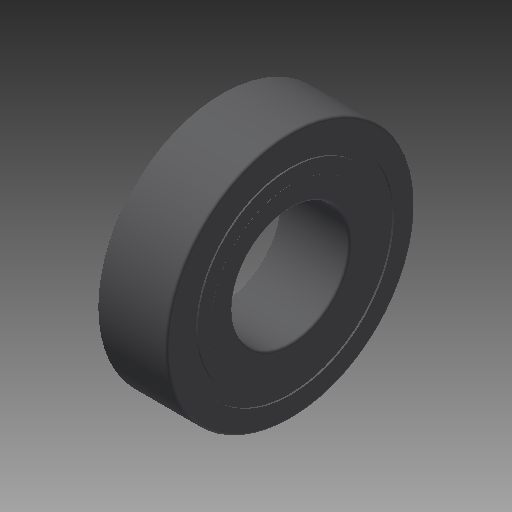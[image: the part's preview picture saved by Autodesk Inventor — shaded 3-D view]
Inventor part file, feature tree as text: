
AUTODESK INVENTOR PART (.ipt)
format: ipt  version: 2018 (Build 220112000, 112)  size: 182,784 bytes
history: native  units: mm
features: other x7, revolve x3, sketch x3
ambient origin geometry x8: Origin, YZ Plane, XZ Plane, XY Plane, X Axis, Y Axis, Z Axis, Center Point
bodies: Solid1 (feature_tree)
feature tree (13):
  revolve  "Revolution1"  Angle=360.0deg
  revolve  "Revolution2"  [1 undecoded]
  revolve  "Revolution3"  [1 undecoded]
  other  "bf_2_XY"
  other  "bf_2_YZ"
  other  "bf_2_ZX"
  other  "bf_2_X"
  other  "bf_2_Y"
  other  "bf_2_Z"
  other  "bf_2_Center"
  sketch  "Sketch_1"  dims[d0=360.0deg d1=360.0deg]
  sketch  "Sketch_2"  dims[d2=360.0deg]
  sketch  "Sketch_3"
note: 2 required parameter values undecoded (feature->parameter linkage not recoverable at this tier; creation-order binding heuristic only, values carry confidence <= 0.55)
